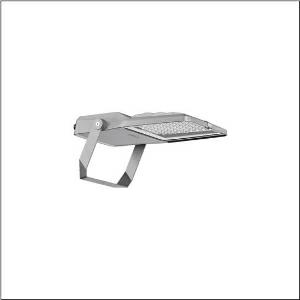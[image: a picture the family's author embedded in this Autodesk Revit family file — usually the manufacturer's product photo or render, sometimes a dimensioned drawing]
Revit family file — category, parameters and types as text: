
# Revit family: floodlight_fl_21_iq_mini___pl64_5xa7772c5e1a_f6c6
name_source: partatom
category: Lighting Fixtures
units: mm (PartAtom-declared; Revit-internal decimal feet)

## family parameters
Cut with Voids When Loaded = No
Host = Face
Light Source = No
Part Type = Normal
Room Calculation Point = No
Round Connector Dimension = Use Diameter
Shared = No

## types (1)
- --- (1 x LED, 11000 lm, 87.2 W, 4000K)
    Apparent Load = 87 VA
    CIE Flux Codes = 28 80 98 100 100
    Color Rendering = 80
    Color Temperature = 4000K
    Default Elevation = 1800 mm
    Description = Floodlight FL 21 iQ mini, floodlight, primary light control with lens, of PMMA, primary optical cover: protective disc, of toughened safety glass, transparent, light distribution: PL64, light emission: direct distribution, installation type: surface-mounted, lamps: LED, High Power LED, rated values: 11.000lm | 87,2W | 126,1lm/W (begin service life); end service life: 11.000lm | 92,1W; at 50% lumin. flux: 5.500lm | 40,1W | 137,2lm/W, colour temperature: 4000K, colour rendering: CRI > 80, light colour: 840, light setting 1 begin service life: 100% | 11.000lm | 87,2W | 126,1lm/W | 4.000K, light setting 1 end service life: 92,1W, further light settings possible, control: Street-Remote, Auto-Match, Temp-Guard, Night-Set, Smart-Wire, Desk-Remote (wireless, voltage-free reading and setting of iQ features in the workshop via application-optimized NFC function/RFID function), optimised constant luminous flux control (CLO 2.0), pre-setting: linear dimming characteristic, with terminal, 6-pole, mains connection: 220..240V, AC, 50/60Hz, luminaire housing, of diecast aluminium, powder-coated, SITECO metallic grey (DB 702S), corrosivity category C5 mid according to DIN EN ISO 12944suitable for swimming poolschlorine-resistant, sealing non-destructively replaceable, mounting bracket, of steel, galvanised, powder-coated, SITECO metallic grey (DB 702S), protection rating (complete): IP66, insulation class (complete): insulation class II (safety insulation), certification: CE, ENEC, VDE, protection symbol: D, impact resistance: IK08, permissible operating ambient temperature: -40..+40°C, permissible operating ambient temperature for outdoor applications: -40..+50°C, standard: DIN EN 12944, LABS conformity tested according to VDMA 24364:2018-05, packaging unit: 1 piece

Light Distribution: PL64
    Height = 70 mm
    Lamp = 1 x LED
    Lamp Light Flux = 11000 lm
    Lamp Power = 87.2 W
    Lamp count = 1
    Length = 485 mm
    Luminous efficacy = 126 lm/W
    Manufacturer = Siteco
    ModVariant = No
    Model = 5XA7772C5E1A
    Number of Poles = 1
    OnlyDefault = Yes
    Power Factor = 1
    Product Name = Floodlight FL 21 iQ mini | PL64
    Product group = floodlight | pylon annexe
    ProductGroupID = 6201
    Protection Class = Protection class II
    Protection Degree = IP 66
    RLX_Detail_Level = 1
    RLX_Emergency_Light_Flux = 0 lm
    RLX_Emergency_Type = 0
    RLX_Emergency_Type_DB = No
    RlxData = <blob elided: 96701 chars, md5=10388043>
    Socket = socket
    Standby Power = 0 W
    System Light Flux = 11000 lm
    System Power = 87 W
    Type Comments = factory setting: luminous flux: 100 % | dim-lin: 254 | 456 mA
    Type Image = l_1006845.jpg
    URL = http://relux.com
    VarID = @adj_165659
    Voltage = 0 V
    Weight = 0.00 kg
    Width = 337 mm

## geometry (parser evidence)
native form markers: Blend x4, Sweep x12
no freeform markers — native parametric forms only
